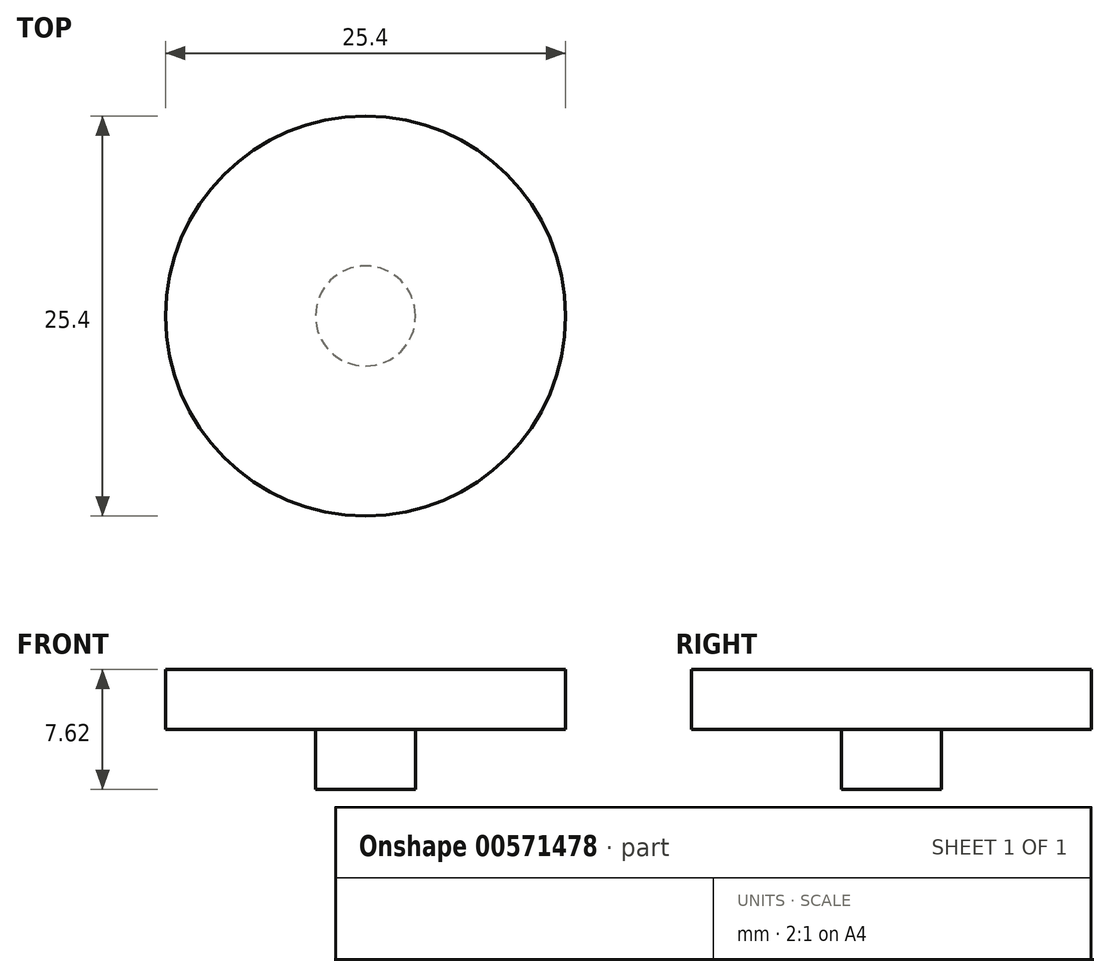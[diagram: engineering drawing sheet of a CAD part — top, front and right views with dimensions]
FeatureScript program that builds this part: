
annotation { "Feature Type Name" : "Feature", "Feature Type Description" : "" }
export const myFeature = defineFeature(function(context is Context, id is Id, definition is map)
    precondition{}
    {
        {
            var Q0;
            Q0=qCreatedBy(makeId("Top.planeOp"),FACE);
            var sketch = newSketch(context, id + "F0", { "sketchPlane" : qUnion([Q0])});
            skCircle(sketch, "E0", {"center": v(0, 0) * mm, "radius": 12.7 * mm});
            skCircle(sketch, "E1", {"center": v(0, 0) * mm, "radius": 3.18 * mm});
            skSolve(sketch);
        }
        {
            var Q0;
            Q0 = qSketchRegion(id + "F0", true);
            var Q1;
            Q1=makeQuery(id+"F0.imprint","IMPRINT",FACE,{"disambiguationData":[TD([[makeQuery(id+"F0.imprint","IMPRINT",EDGE,{"derivedFrom":sQuery(id+"F0.wireOp",EDGE,"E1")}),1.0]])]});
            extrude(context, id + "F1", {"entities" : qUnion([Q0, Q1]), "depth" : 3.8 * mm, "offsetDistance" : 25.4 * mm});
        }
        {
            var Q0;
            Q0=makeQuery(id+"F0.imprint","IMPRINT",FACE,{"disambiguationData":[TD([[makeQuery(id+"F0.imprint","IMPRINT",EDGE,{"derivedFrom":sQuery(id+"F0.wireOp",EDGE,"E1")}),1.0]])]});
            extrude(context, id + "F2", {"entities" : qUnion([Q0]), "operationType" : NewBodyOperationType.ADD, "oppositeDirection" : true, "depth" : 3.8 * mm, "offsetDistance" : 25.4 * mm});
        }
    });
